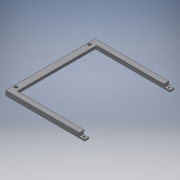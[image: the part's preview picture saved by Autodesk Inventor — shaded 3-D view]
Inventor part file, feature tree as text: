
AUTODESK INVENTOR PART (.ipt)
format: ipt  version: 2016 SP2 (Build 200236200, 236)  size: 167,936 bytes
history: native  units: mm
features: extrude x5, sketch x5, projected_geometry x4
ambient origin geometry x8: Origin, YZ Plane, XZ Plane, XY Plane, X Axis, Y Axis, Z Axis, Center Point
bodies: Volumenkörper1 (feature_tree)
feature tree (14):
  extrude  "Extrusion1"  Depth=9.5mm
  extrude  "Extrusion2"  Depth=150.5mm
  extrude  "Extrusion3"  Depth=1.2mm TaperAngle=0.0deg
  extrude  "Extrusion4"  Depth=8.0mm
  extrude  "Extrusion5"  Depth=8.0mm
  sketch  "Skizze1"  dims[d0=9.5mm d1=9.5mm]
  sketch  "Skizze2"  dims[d2=12.0mm d3=150.5mm]
  sketch  "Skizze3"  dims[d4=127.4mm d5=1.2mm d6=0.0mm]
  projected_geometry  "Projizierte Kontur1"
  projected_geometry  "Projizierte Kontur2"
  sketch  "Skizze4"  dims[d7=10.0mm d8=8.0mm]
  sketch  "Skizze5"  dims[d9=8.0mm d10=8.0mm d11=3.0mm d12=5.0mm d13=4.0mm d14=3.0mm d15=5.0mm d16=4.0mm d17=7.7mm d18=0.0mm d19=5.1mm d20=0.0mm d21=4.0mm d22=5.7mm d23=5.7mm d24=15.0mm d25=15.0mm d26=3.1mm d27=0.0mm d28=3.0mm d29=3.0mm d30=42.55mm d31=0.0mm]
  projected_geometry  "Projizierte Kontur3"
  projected_geometry  "Projizierte Kontur4"
